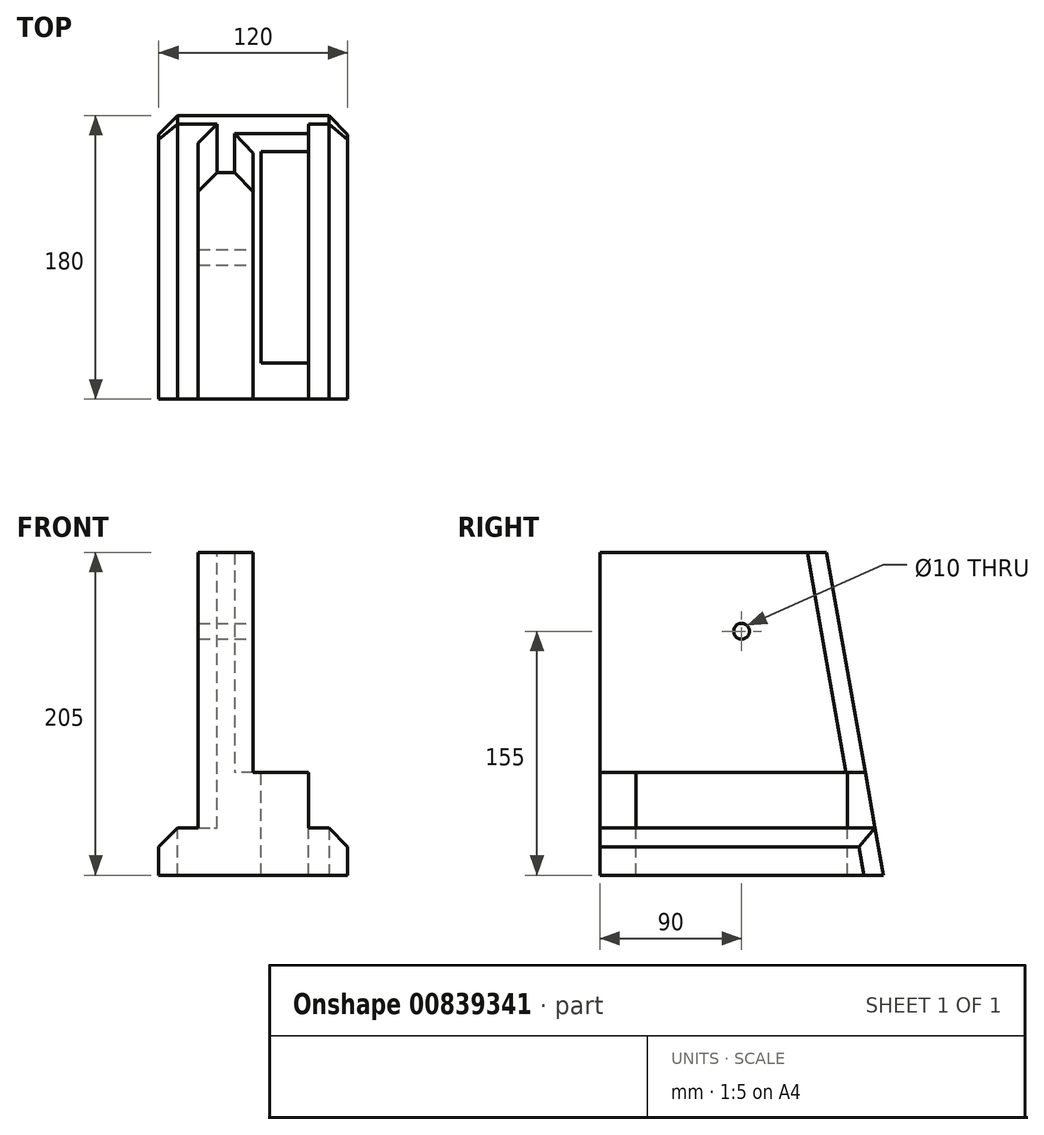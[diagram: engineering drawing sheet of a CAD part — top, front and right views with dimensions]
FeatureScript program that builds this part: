
annotation { "Feature Type Name" : "Feature", "Feature Type Description" : "" }
export const myFeature = defineFeature(function(context is Context, id is Id, definition is map)
    precondition{}
    {
        {
            var Q0;
            Q0=qCreatedBy(makeId("Front.planeOp"),FACE);
            var sketch = newSketch(context, id + "F0", { "sketchPlane" : qUnion([Q0])});
            skLineSegment(sketch, "E0", {"start": v(0, 292.25) * mm, "end": v(0, 65.22) * mm, "construction": true});
            skLineSegment(sketch, "E1", {"start": v(0, 205) * mm, "end": v(-35, 205) * mm});
            skLineSegment(sketch, "E2", {"start": v(-35, 205) * mm, "end": v(-35, 30) * mm});
            skLineSegment(sketch, "E3", {"start": v(-35, 30) * mm, "end": v(-60, 30) * mm});
            skLineSegment(sketch, "E4", {"start": v(-60, 30) * mm, "end": v(-60, 0) * mm});
            skLineSegment(sketch, "E5", {"start": v(-60, 0) * mm, "end": v(0, 0) * mm});
            skLineSegment(sketch, "E6.MirrorCS", {"start": v(60, 30) * mm, "end": v(60, 0) * mm});
            skLineSegment(sketch, "E7.MirrorCS", {"start": v(60, 0) * mm, "end": v(0, 0) * mm});
            skPoint(sketch, "E8.MirrorCS.start.orphan", {"position": v(35, 205) * mm});
            skPoint(sketch, "E9.MirrorCS.start.orphan", {"position": v(0, 205) * mm});
            skPoint(sketch, "E10.MirrorCS.end.orphan", {"position": v(60, 30) * mm});
            skLineSegment(sketch, "E11", {"start": v(60, 30) * mm, "end": v(35, 30) * mm});
            skLineSegment(sketch, "E12", {"start": v(0, 205) * mm, "end": v(0, 205) * mm});
            skLineSegment(sketch, "E13", {"start": v(0, 205) * mm, "end": v(0, 65.22) * mm});
            skPoint(sketch, "E14.orphan", {"position": v(0, 30) * mm});
            skLineSegment(sketch, "E15", {"start": v(0, 65.22) * mm, "end": v(35, 65.22) * mm});
            skLineSegment(sketch, "E16", {"start": v(35, 65.22) * mm, "end": v(35, 30) * mm});
            skLineSegment(sketch, "E17.trimOffspring", {"start": v(0, 0) * mm, "end": v(0, -375.47) * mm, "construction": true});
            skSolve(sketch);
        }
        {
            var Q0;
            Q0 = qSketchRegion(id + "F0", true);
            extrude(context, id + "F1", {"entities" : qUnion([Q0]), "endBound" : BoundingType.SYMMETRIC, "depth" : 180 * mm, "offsetDistance" : 25 * mm});
        }
        {
            var Q0;
            Q0=qCreatedBy(makeId("Right.planeOp"),FACE);
            var sketch = newSketch(context, id + "F2", { "sketchPlane" : qUnion([Q0])});
            skLineSegment(sketch, "E18", {"start": v(0, -8.43) * mm, "end": v(0, 134.15) * mm, "construction": true});
            skCircle(sketch, "E19", {"center": v(0, 155) * mm, "radius": 5 * mm});
            skSolve(sketch);
        }
        {
            var Q0;
            Q0 = qSketchRegion(id + "F2", true);
            extrude(context, id + "F3", {"entities" : qUnion([Q0]), "operationType" : NewBodyOperationType.REMOVE, "endBound" : BoundingType.SYMMETRIC, "oppositeDirection" : true, "depth" : 100 * mm, "offsetDistance" : 25 * mm});
        }
        {
            var Q0;
            Q0=makeQuery(id+"F1.opExtrude","SWEPT_FACE",FACE,{"disambiguationData":[OSD([sQuery(id+"F0.wireOp",EDGE,"E11")])]});
            var sketch = newSketch(context, id + "F4", { "sketchPlane" : qUnion([Q0])});
            skLineSegment(sketch, "E20", {"start": v(47.5, -90) * mm, "end": v(47.5, -67.07) * mm, "construction": true});
            skLineSegment(sketch, "E21", {"start": v(67.42, 0) * mm, "end": v(-13.85, 0) * mm, "construction": true});
            skLineSegment(sketch, "E22.0", {"start": v(5, -67.07) * mm, "end": v(5, 67.07) * mm});
            skPoint(sketch, "E23.orphan", {"position": v(5, -90) * mm});
            skPoint(sketch, "E24.orphan", {"position": v(5, 90) * mm});
            skLineSegment(sketch, "E25.trimOffspring", {"start": v(47.5, 0) * mm, "end": v(47.5, 90) * mm, "construction": true});
            skLineSegment(sketch, "E26", {"start": v(47.5, -67.07) * mm, "end": v(47.5, 0) * mm, "construction": true});
            skLineSegment(sketch, "E27", {"start": v(5, -67.07) * mm, "end": v(41.02, -67.07) * mm});
            skLineSegment(sketch, "E28", {"start": v(41.02, -67.07) * mm, "end": v(41.02, 67.07) * mm});
            skLineSegment(sketch, "E29", {"start": v(41.02, 67.07) * mm, "end": v(5, 67.07) * mm});
            skSolve(sketch);
        }
        {
            var Q0;
            Q0=makeQuery(id+"F4.imprint","IMPRINT",FACE,{"disambiguationData":[TD([[makeQuery(id+"F4.imprint","IMPRINT",EDGE,{"derivedFrom":sQuery(id+"F4.wireOp",EDGE,"E22.0")}),-1.0]])]});
            extrude(context, id + "F5", {"entities" : qUnion([Q0]), "operationType" : NewBodyOperationType.REMOVE, "endBound" : BoundingType.SYMMETRIC, "oppositeDirection" : true, "depth" : 80 * mm, "offsetDistance" : 25 * mm});
        }
        {
            var Q0;
            Q0=makeQuery(id+"F1.opExtrude","CAP_EDGE",EDGE,{"disambiguationData":[OSD([sQuery(id+"F0.wireOp",EDGE,"E5"),sQuery(id+"F0.wireOp",EDGE,"E7.MirrorCS")])],"isStart":true});
            cPlane(context, id + "F6", {"entities" : qUnion([Q0]), "cplaneType" : CPlaneType.LINE_ANGLE, "offset" : 0 * mm, "angle" : 10 * degree, "width" : 150 * mm, "height" : 150 * mm});
        }
        {
            var Q0;
            Q0=qCreatedBy(id+"F6.planeOp",FACE);
            var sketch = newSketch(context, id + "F7", { "sketchPlane" : qUnion([Q0])});
            skLineSegment(sketch, "E30.bottom", {"start": v(165.06, -63.68) * mm, "end": v(-144, -63.68) * mm});
            skLineSegment(sketch, "E30.top", {"start": v(165.06, 230.07) * mm, "end": v(-144, 230.07) * mm});
            skLineSegment(sketch, "E30.left", {"start": v(165.06, -63.68) * mm, "end": v(165.06, 230.07) * mm});
            skLineSegment(sketch, "E30.right", {"start": v(-144, -63.68) * mm, "end": v(-144, 230.07) * mm});
            skSolve(sketch);
        }
        {
            var Q0;
            Q0 = qSketchRegion(id + "F7", true);
            extrude(context, id + "F8", {"entities" : qUnion([Q0]), "operationType" : NewBodyOperationType.REMOVE, "depth" : 60 * mm, "offsetDistance" : 25 * mm});
        }
        {
            var Q0;
            Q0=makeQuery(id+"FJ1BTQ4dWtdMG3B_1.1.F8.boolean.opBoolean","INTERSECT",EDGE,{"derivedFrom":[makeQuery(id+"F1.opExtrude","SWEPT_FACE",FACE,{"disambiguationData":[OSD([sQuery(id+"F0.wireOp",EDGE,"E4")])]}),makeQuery(id+"FJ1BTQ4dWtdMG3B_1.1.F8.opExtrude","CAP_FACE",FACE,{"disambiguationData":[OSD([sQuery(id+"F7.wireOp",EDGE,"E30.bottom"),sQuery(id+"F7.wireOp",EDGE,"E30.top"),sQuery(id+"F7.wireOp",EDGE,"E30.left"),sQuery(id+"F7.wireOp",EDGE,"E30.right")])],"isStart":true})]});
            var Q1;
            Q1=makeQuery(id+"FJ1BTQ4dWtdMG3B_1.1.F8.boolean.opBoolean","INTERSECT",EDGE,{"derivedFrom":[makeQuery(id+"F1.opExtrude","SWEPT_FACE",FACE,{"disambiguationData":[OSD([sQuery(id+"F0.wireOp",EDGE,"E6.MirrorCS")])]}),makeQuery(id+"FJ1BTQ4dWtdMG3B_1.1.F8.opExtrude","CAP_FACE",FACE,{"disambiguationData":[OSD([sQuery(id+"F7.wireOp",EDGE,"E30.bottom"),sQuery(id+"F7.wireOp",EDGE,"E30.top"),sQuery(id+"F7.wireOp",EDGE,"E30.left"),sQuery(id+"F7.wireOp",EDGE,"E30.right")])],"isStart":true})]});
            var Q2;
            Q2=makeQuery(id+"FJ1BTQ4dWtdMG3B_1.1.F8.boolean.opBoolean","INTERSECT",EDGE,{"derivedFrom":[makeQuery(id+"F1.opExtrude","SWEPT_FACE",FACE,{"disambiguationData":[OSD([sQuery(id+"F0.wireOp",EDGE,"E2")])]}),makeQuery(id+"FJ1BTQ4dWtdMG3B_1.1.F8.opExtrude","CAP_FACE",FACE,{"disambiguationData":[OSD([sQuery(id+"F7.wireOp",EDGE,"E30.bottom"),sQuery(id+"F7.wireOp",EDGE,"E30.top"),sQuery(id+"F7.wireOp",EDGE,"E30.left"),sQuery(id+"F7.wireOp",EDGE,"E30.right")])],"isStart":true})]});
            var Q3;
            Q3=makeQuery(id+"FJ1BTQ4dWtdMG3B_1.1.F8.boolean.opBoolean","INTERSECT",EDGE,{"derivedFrom":[makeQuery(id+"F1.opExtrude","SWEPT_FACE",FACE,{"disambiguationData":[OSD([sQuery(id+"F0.wireOp",EDGE,"E13")])]}),makeQuery(id+"FJ1BTQ4dWtdMG3B_1.1.F8.opExtrude","CAP_FACE",FACE,{"disambiguationData":[OSD([sQuery(id+"F7.wireOp",EDGE,"E30.bottom"),sQuery(id+"F7.wireOp",EDGE,"E30.top"),sQuery(id+"F7.wireOp",EDGE,"E30.left"),sQuery(id+"F7.wireOp",EDGE,"E30.right")])],"isStart":true})]});
            var Q4;
            Q4=makeQuery(id+"F8.boolean.opBoolean","INTERSECT",EDGE,{"derivedFrom":[makeQuery(id+"F1.opExtrude","SWEPT_FACE",FACE,{"disambiguationData":[OSD([sQuery(id+"F0.wireOp",EDGE,"E13")])]}),makeQuery(id+"F8.opExtrude","CAP_FACE",FACE,{"disambiguationData":[OSD([sQuery(id+"F7.wireOp",EDGE,"E30.bottom"),sQuery(id+"F7.wireOp",EDGE,"E30.top"),sQuery(id+"F7.wireOp",EDGE,"E30.left"),sQuery(id+"F7.wireOp",EDGE,"E30.right")])],"isStart":true})]});
            var Q5;
            Q5=makeQuery(id+"F8.boolean.opBoolean","INTERSECT",EDGE,{"derivedFrom":[makeQuery(id+"F1.opExtrude","SWEPT_FACE",FACE,{"disambiguationData":[OSD([sQuery(id+"F0.wireOp",EDGE,"E2")])]}),makeQuery(id+"F8.opExtrude","CAP_FACE",FACE,{"disambiguationData":[OSD([sQuery(id+"F7.wireOp",EDGE,"E30.bottom"),sQuery(id+"F7.wireOp",EDGE,"E30.top"),sQuery(id+"F7.wireOp",EDGE,"E30.left"),sQuery(id+"F7.wireOp",EDGE,"E30.right")])],"isStart":true})]});
            var Q6;
            Q6=makeQuery(id+"F8.boolean.opBoolean","INTERSECT",EDGE,{"derivedFrom":[makeQuery(id+"F1.opExtrude","SWEPT_FACE",FACE,{"disambiguationData":[OSD([sQuery(id+"F0.wireOp",EDGE,"E4")])]}),makeQuery(id+"F8.opExtrude","CAP_FACE",FACE,{"disambiguationData":[OSD([sQuery(id+"F7.wireOp",EDGE,"E30.bottom"),sQuery(id+"F7.wireOp",EDGE,"E30.top"),sQuery(id+"F7.wireOp",EDGE,"E30.left"),sQuery(id+"F7.wireOp",EDGE,"E30.right")])],"isStart":true})]});
            var Q7;
            Q7=makeQuery(id+"F8.boolean.opBoolean","INTERSECT",EDGE,{"derivedFrom":[makeQuery(id+"F1.opExtrude","SWEPT_FACE",FACE,{"disambiguationData":[OSD([sQuery(id+"F0.wireOp",EDGE,"E6.MirrorCS")])]}),makeQuery(id+"F8.opExtrude","CAP_FACE",FACE,{"disambiguationData":[OSD([sQuery(id+"F7.wireOp",EDGE,"E30.bottom"),sQuery(id+"F7.wireOp",EDGE,"E30.top"),sQuery(id+"F7.wireOp",EDGE,"E30.left"),sQuery(id+"F7.wireOp",EDGE,"E30.right")])],"isStart":true})]});
            var Q8;
            Q8=makeQuery(id+"F1.opExtrude","SWEPT_EDGE",EDGE,{"disambiguationData":[OSD([sQuery(id+"F0.wireOp",EDGE,"E3"),sQuery(id+"F0.wireOp",EDGE,"E4")])]});
            var Q9;
            Q9=makeQuery(id+"F1.opExtrude","SWEPT_EDGE",EDGE,{"disambiguationData":[OSD([sQuery(id+"F0.wireOp",EDGE,"E6.MirrorCS"),sQuery(id+"F0.wireOp",EDGE,"E11")])]});
            chamfer(context, id + "F9", {"entities" : qUnion([Q0, Q1, Q2, Q3, Q4, Q5, Q6, Q7, Q8, Q9]), "width" : 12 * mm, "tangentPropagation" : true});
        }
    });
